# Revit family: Reece_Mirror_ISSY_Z8 Butterfly
name_source: partatom
category: Casework
revit_build: Autodesk Revit 2018 (Build: 20190510_1515(x64)
units: mm (PartAtom-declared; Revit-internal decimal feet)

## family parameters
Cut with Voids When Loaded = Yes
Host = Face
Room Calculation Point = Yes
Shared = Yes

## types (1)
- Reece_All Types
    Default Elevation = 0 mm  [stored 0 ft]
    Depth = 150 mm  [stored 0.492126 ft]
    Description = -
    Disclaimer = THIS FILE IS THE PROPERTY OF THE REECE GROUP. IT MAY NOT BE REPRODUCED, REVERSE-ENGINEERED OR MODIFIED. ANY REPUBLICATION, TRANSMISSION OR DISTRIBUTION FOR THE PURPOSE OF COMMERCIALLY EXPLOITING THE FILES IS PROHIBITED.
    Finish = Please refer to Colour, Finish and Material Variations Document for more information.
    Height = 930 mm  [stored 3.05118 ft]
    Height_Min = 930 mm  [stored 3.05118 ft]
    Keynote = Product #, Reece_Mirror_ISSY_Z8 Butterfly - Reece_All Types
    Manufacturer = -
    Model = -
    Reece_Cabinet_Mirror_Visibility = Yes
    Reece_Cabinet_Offset = 0 mm  [stored 0 ft]
    Reece_Custom_Unit = No
    Reece_Detail_Disclaimer = THIS FILE IS THE PROPERTY OF THE REECE GROUP. IT MAY NOT BE REPRODUCED, REVERSE-ENGINEERED OR MODIFIED. ANY REPUBLICATION, TRANSMISSION OR DISTRIBUTION FOR THE PURPOSE OF COMMERCIALLY EXPLOITING THE FILES IS PROHIBITED.
    Reece_Detail_Material = Please refer to Colour, Finish and Material Variations Document for more information.
    Reece_Divider_Visibility = No
    Reece_Fixed_Height = 930 mm  [stored 3.05118 ft]
    Reece_Fixed_Width = 500 mm  [stored 1.64042 ft]
    Reece_Material_Cabinet = Reece_Veneer_Oak_American
    Reece_Material_Main = Reece_Glass_Mirror
    Reece_Material_Secondary = Reece_Oak_American
    Reece_Material_Shelf = Reece_Veneer_Oak_American
    Reece_Mirror_Depth = 23 mm  [stored 0.0754593 ft]
    Reece_Mirror_Only_Visibility = No
    Reece_Non_Recessed = Yes
    Reece_Overall_Depth = 150 mm  [stored 0.492126 ft]
    Reece_Panel_Count = 1
    Reece_Panel_Count_Number = 1
    Reece_Product_Finishes_Web Page = https://digitalassets.reecegroup.com.au
    Reece_Recessed = No
    Reece_Single_Compartment = No
    Reece_Split_Batten_Visibility = No
    Type Comments = -
    URL = -
    Width = 500 mm  [stored 1.64042 ft]
    Width_Min = 500 mm  [stored 1.64042 ft]

note: [stored X ft] marks values corroborated as IEEE doubles in the binary element streams (Revit-internal decimal feet)

## geometry (parser evidence)
native form markers: Sweep x8
no freeform markers — native parametric forms only
